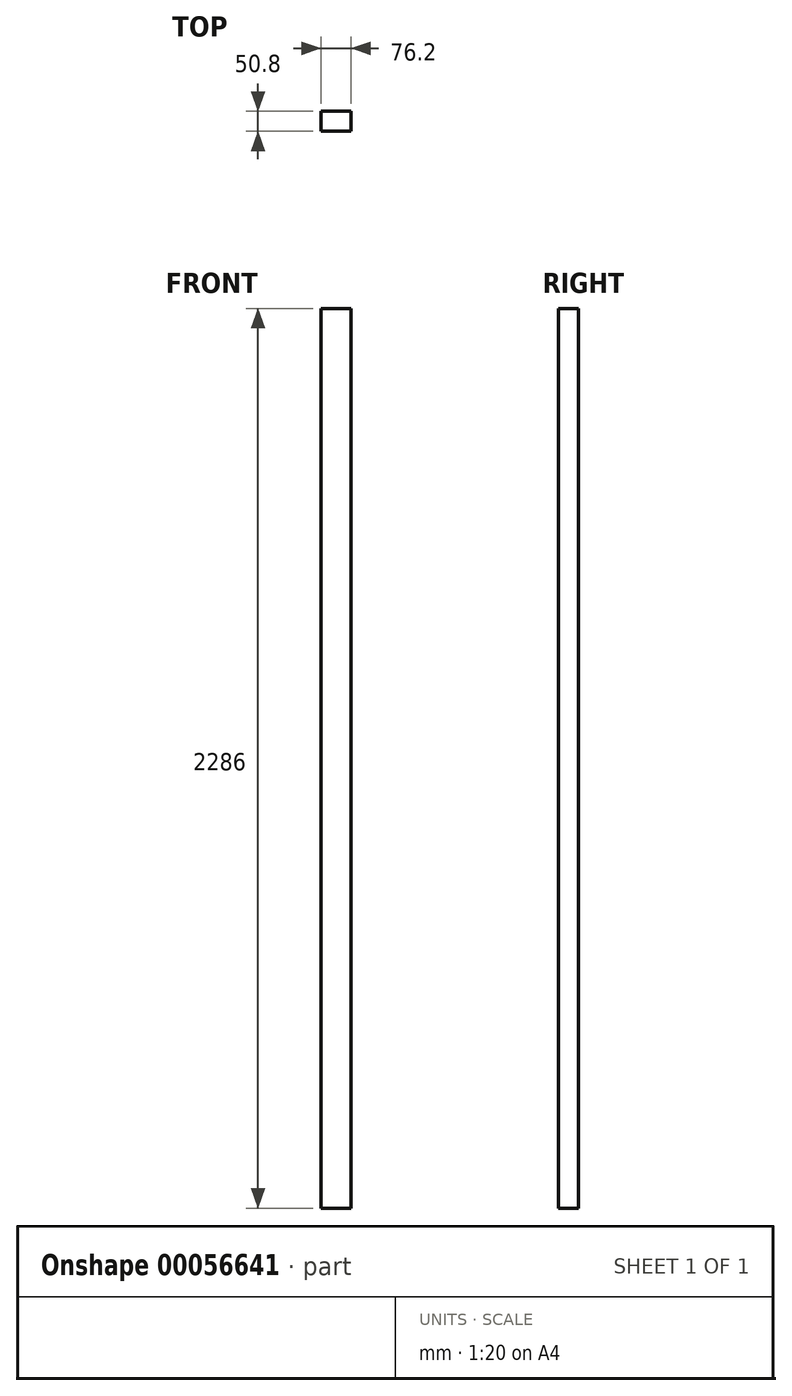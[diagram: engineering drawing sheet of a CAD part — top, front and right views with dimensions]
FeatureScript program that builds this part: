
annotation { "Feature Type Name" : "Feature", "Feature Type Description" : "" }
export const myFeature = defineFeature(function(context is Context, id is Id, definition is map)
    precondition{}
    {
        {
            var Q0;
            Q0=qCreatedBy(makeId("Front.planeOp"),FACE);
            var sketch = newSketch(context, id + "F0", { "sketchPlane" : qUnion([Q0])});
            skLineSegment(sketch, "E0.bottom", {"start": v(-131.2, 1138.85) * mm, "end": v(-55, 1138.85) * mm});
            skLineSegment(sketch, "E0.top", {"start": v(-131.2, -1147.15) * mm, "end": v(-55, -1147.15) * mm});
            skLineSegment(sketch, "E0.left", {"start": v(-131.2, 1138.85) * mm, "end": v(-131.2, -1147.15) * mm});
            skLineSegment(sketch, "E0.right", {"start": v(-55, 1138.85) * mm, "end": v(-55, -1147.15) * mm});
            skSolve(sketch);
        }
        {
            var Q0;
            Q0 = qSketchRegion(id + "F0", true);
            extrude(context, id + "F1", {"entities" : qUnion([Q0]), "oppositeDirection" : true, "depth" : 50.8 * mm});
        }
    });
